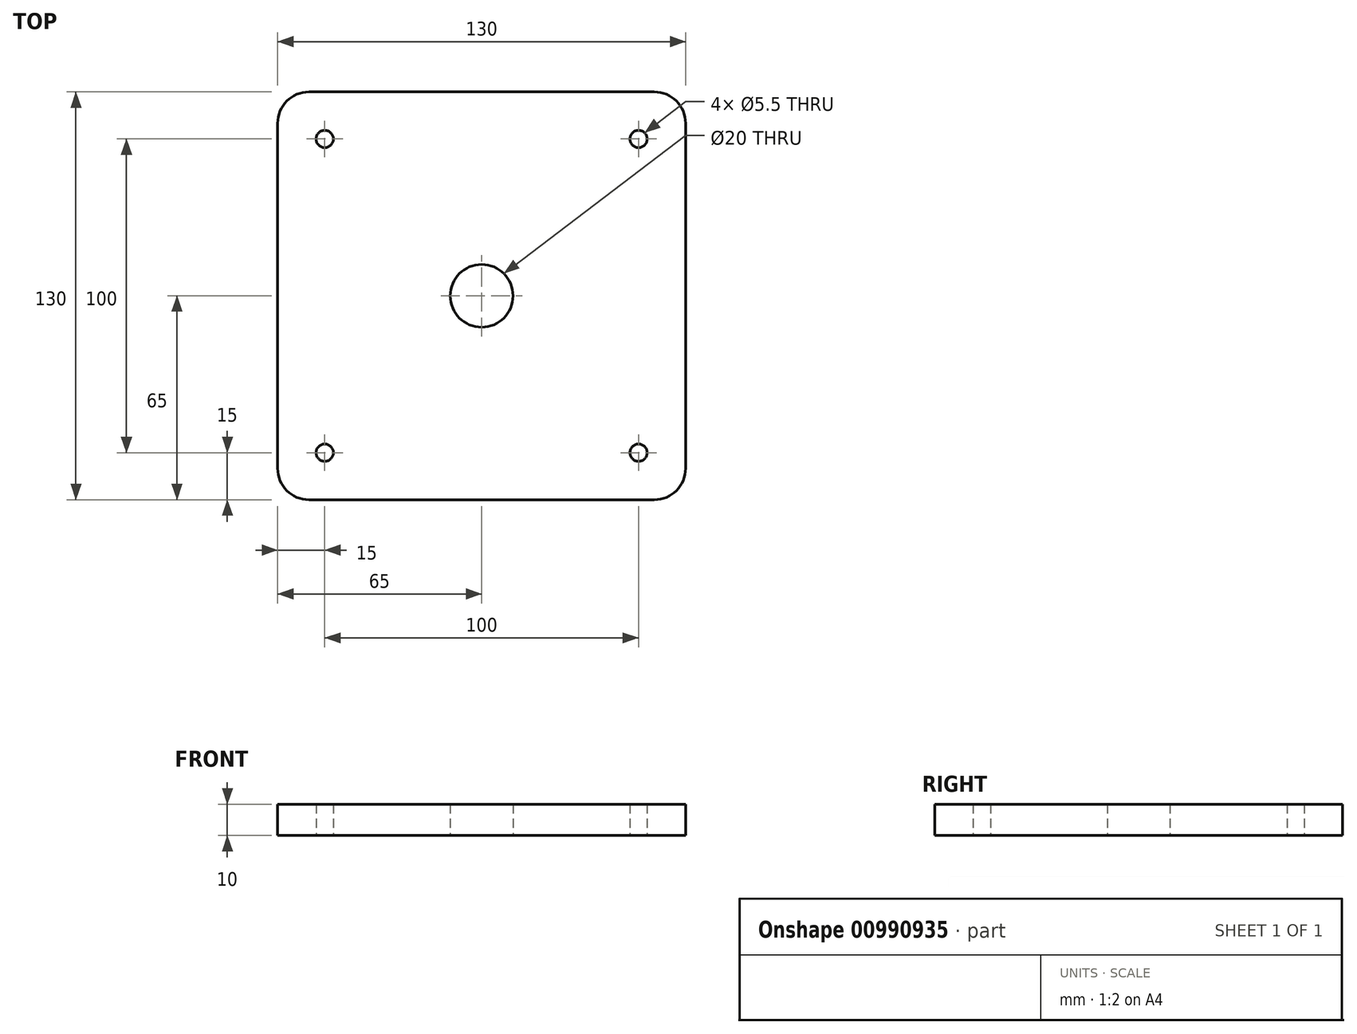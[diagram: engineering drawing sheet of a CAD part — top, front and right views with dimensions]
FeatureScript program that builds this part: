
annotation { "Feature Type Name" : "Feature", "Feature Type Description" : "" }
export const myFeature = defineFeature(function(context is Context, id is Id, definition is map)
    precondition{}
    {
        {
            var Q0;
            Q0=qCreatedBy(makeId("Top.planeOp"),FACE);
            var sketch = newSketch(context, id + "F0", { "sketchPlane" : qUnion([Q0])});
            skLineSegment(sketch, "E0.bottom", {"start": v(55, -65) * mm, "end": v(-55, -65) * mm});
            skLineSegment(sketch, "E0.top", {"start": v(55, 65) * mm, "end": v(-55, 65) * mm});
            skLineSegment(sketch, "E0.left", {"start": v(65, -55) * mm, "end": v(65, 55) * mm});
            skLineSegment(sketch, "E0.right", {"start": v(-65, -55) * mm, "end": v(-65, 55) * mm});
            skPoint(sketch, "E0.middle", {"position": v(0, 0) * mm});
            skCircle(sketch, "E1", {"center": v(-50, 50) * mm, "radius": 2.75 * mm});
            skCircle(sketch, "E2.MirrorC", {"center": v(50, 50) * mm, "radius": 2.75 * mm});
            skCircle(sketch, "E3.MirrorC", {"center": v(-50, -50) * mm, "radius": 2.75 * mm});
            skCircle(sketch, "E4.MirrorC", {"center": v(50, -50) * mm, "radius": 2.75 * mm});
            skPoint(sketch, "E5.visualSharp", {"position": v(-65, 65) * mm});
            skArc(sketch, "E5.filletArc", {"start": v(-55, 65) * mm, "mid": v(-62.07, 62.07) * mm, "end": v(-65, 55) * mm});
            skPoint(sketch, "E6.visualSharp", {"position": v(65, 65) * mm});
            skArc(sketch, "E6.filletArc", {"start": v(65, 55) * mm, "mid": v(62.07, 62.07) * mm, "end": v(55, 65) * mm});
            skPoint(sketch, "E7.visualSharp", {"position": v(65, -65) * mm});
            skArc(sketch, "E7.filletArc", {"start": v(55, -65) * mm, "mid": v(62.07, -62.07) * mm, "end": v(65, -55) * mm});
            skPoint(sketch, "E8.visualSharp", {"position": v(-65, -65) * mm});
            skArc(sketch, "E8.filletArc", {"start": v(-65, -55) * mm, "mid": v(-62.07, -62.07) * mm, "end": v(-55, -65) * mm});
            skCircle(sketch, "E9", {"center": v(0, 0) * mm, "radius": 10 * mm});
            skSolve(sketch);
        }
        {
            var Q0;
            Q0 = qSketchRegion(id + "F0", true);
            extrude(context, id + "F1", {"entities" : qUnion([Q0]), "depth" : 10 * mm, "offsetDistance" : 25 * mm});
        }
    });
